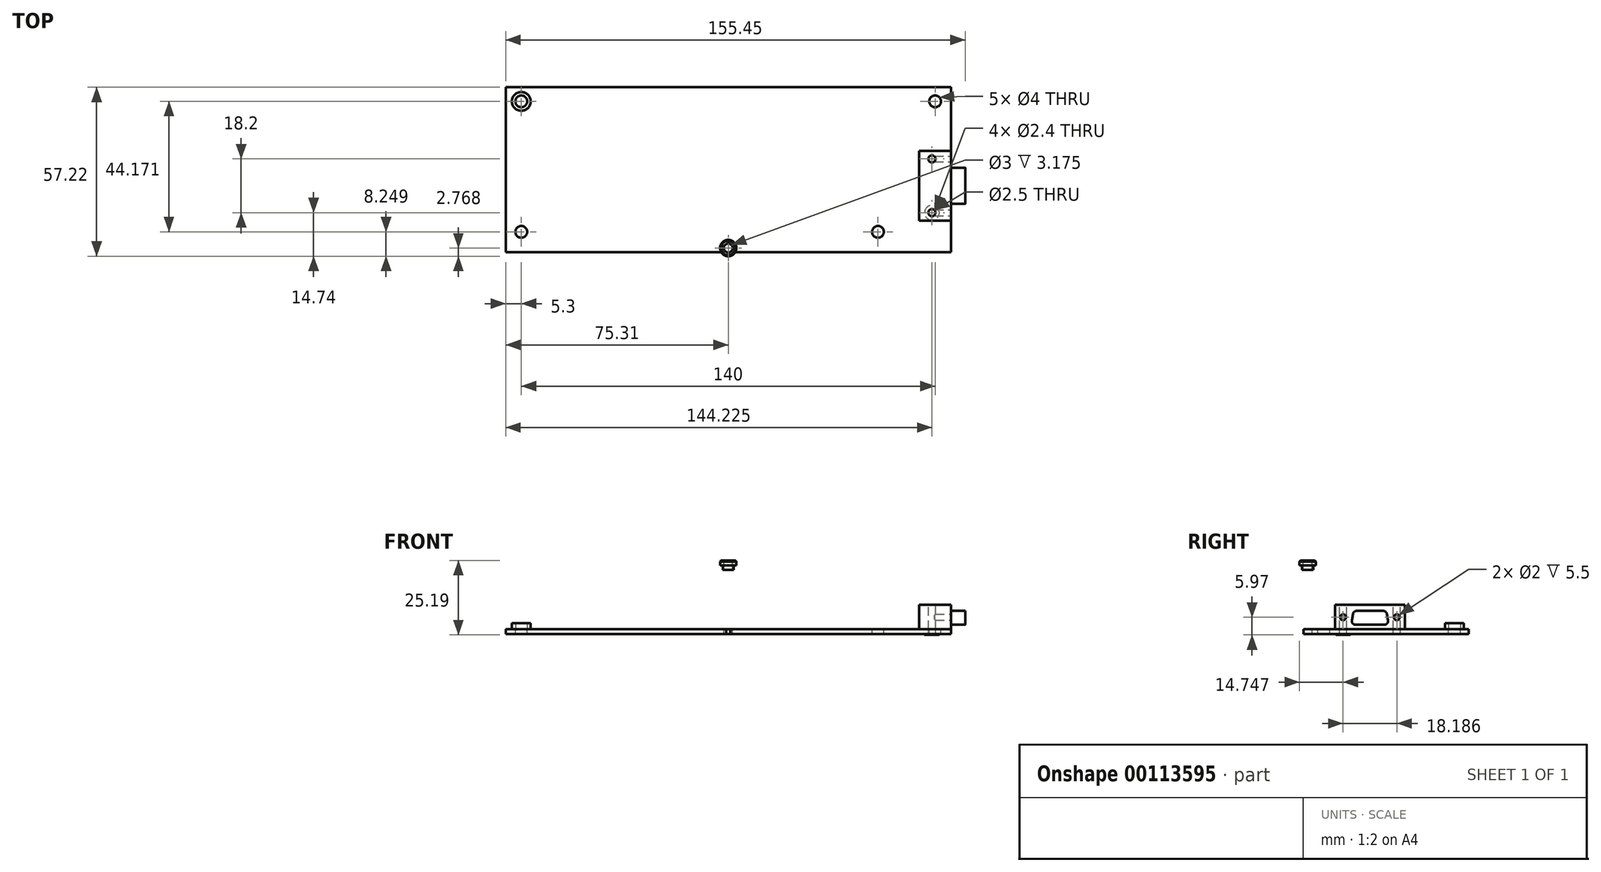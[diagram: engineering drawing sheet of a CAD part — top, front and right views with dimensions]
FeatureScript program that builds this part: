
annotation { "Feature Type Name" : "Feature", "Feature Type Description" : "" }
export const myFeature = defineFeature(function(context is Context, id is Id, definition is map)
    precondition{}
    {
        {
            var Q0;
            Q0=qCreatedBy(makeId("Top.planeOp"),FACE);
            var sketch = newSketch(context, id + "F0", { "sketchPlane" : qUnion([Q0])});
            skLineSegment(sketch, "E0.bottom", {"start": v(75.3, -55.8) * mm, "end": v(-75.31, -55.8) * mm});
            skLineSegment(sketch, "E0.top", {"start": v(75.31, 0) * mm, "end": v(-75.31, 0) * mm});
            skLineSegment(sketch, "E0.left", {"start": v(75.31, -55.8) * mm, "end": v(75.31, 0) * mm});
            skLineSegment(sketch, "E0.right", {"start": v(-75.31, -55.8) * mm, "end": v(-75.31, 0) * mm});
            skPoint(sketch, "E0.middle", {"position": v(0, -27.9) * mm});
            skLineSegment(sketch, "E1", {"start": v(0, 0) * mm, "end": v(0, -55.8) * mm, "construction": true});
            skCircle(sketch, "E2", {"center": v(-70.01, -4.8) * mm, "radius": 2 * mm});
            skCircle(sketch, "E3", {"center": v(-70.01, -48.97) * mm, "radius": 2 * mm});
            skCircle(sketch, "E4", {"center": v(70, -4.8) * mm, "radius": 2 * mm});
            skCircle(sketch, "E5", {"center": v(50.66, -48.97) * mm, "radius": 2 * mm});
            skSolve(sketch);
        }
        {
            var Q0;
            Q0 = qSketchRegion(id + "F0", true);
            extrude(context, id + "F1", {"entities" : qUnion([Q0]), "oppositeDirection" : true, "depth" : 1.57 * mm});
        }
        {
            var Q0;
            Q0=qCreatedBy(makeId("Top.planeOp"),FACE);
            var sketch = newSketch(context, id + "F2", { "sketchPlane" : qUnion([Q0])});
            skCircle(sketch, "E6", {"center": v(-70.01, -4.8) * mm, "radius": 2 * mm});
            skCircle(sketch, "E7", {"center": v(-70.01, -4.8) * mm, "radius": 3.17 * mm});
            skSolve(sketch);
        }
        {
            var Q0;
            Q0 = qSketchRegion(id + "F2", true);
            extrude(context, id + "F3", {"entities" : qUnion([Q0]), "depth" : 2.03 * mm});
        }
        {
            var Q0;
            Q0=makeQuery(id+"F1.opExtrude","CAP_FACE",FACE,{"disambiguationData":[OSD([sQuery(id+"F0.wireOp",EDGE,"E0.bottom"),sQuery(id+"F0.wireOp",EDGE,"E0.top"),sQuery(id+"F0.wireOp",EDGE,"E0.left"),sQuery(id+"F0.wireOp",EDGE,"E0.right"),sQuery(id+"F0.wireOp",EDGE,"E2"),sQuery(id+"F0.wireOp",EDGE,"E3"),sQuery(id+"F0.wireOp",EDGE,"E4"),sQuery(id+"F0.wireOp",EDGE,"E5")])],"isStart":true});
            var sketch = newSketch(context, id + "F4", { "sketchPlane" : qUnion([Q0])});
            skLineSegment(sketch, "E8.bottom", {"start": v(64.52, -21.62) * mm, "end": v(75.31, -21.62) * mm});
            skLineSegment(sketch, "E8.top", {"start": v(64.52, -45.14) * mm, "end": v(75.31, -45.14) * mm});
            skLineSegment(sketch, "E8.left", {"start": v(64.51, -21.62) * mm, "end": v(64.51, -45.14) * mm});
            skLineSegment(sketch, "E8.right", {"start": v(75.31, -21.62) * mm, "end": v(75.31, -45.14) * mm});
            skLineSegment(sketch, "E9", {"start": v(75.31, -33.38) * mm, "end": v(64.52, -33.38) * mm, "construction": true});
            skPoint(sketch, "E9.endSnap0", {"position": v(64.52, -33.38) * mm});
            skSolve(sketch);
        }
        {
            var Q0;
            Q0 = qSketchRegion(id + "F4", true);
            var Q1;
            Q1=sQuery(id+"F4.wireOp",EDGE,"E9");
            extrude(context, id + "F5", {"entities" : qUnion([Q0]), "surfaceEntities" : qUnion([Q1]), "depth" : 8.29 * mm});
        }
        {
            var Q0;
            Q0=makeQuery(id+"F5.opExtrude","SWEPT_FACE",FACE,{"disambiguationData":[OSD([sQuery(id+"F4.wireOp",EDGE,"E8.right")])]});
            var sketch = newSketch(context, id + "F6", { "sketchPlane" : qUnion([Q0])});
            skLineSegment(sketch, "E10.bottom", {"start": v(-37.88, 6.25) * mm, "end": v(-28.88, 6.25) * mm});
            skLineSegment(sketch, "E10.top", {"start": v(-38.26, 1.55) * mm, "end": v(-28.5, 1.55) * mm});
            skLineSegment(sketch, "E11", {"start": v(-39.13, 5.2) * mm, "end": v(-39.51, 3.04) * mm});
            skLineSegment(sketch, "E12", {"start": v(-27.63, 5.2) * mm, "end": v(-27.25, 3.04) * mm});
            skPoint(sketch, "E13.visualSharp", {"position": v(-38.94, 6.25) * mm});
            skArc(sketch, "E13.filletArc", {"start": v(-37.88, 6.25) * mm, "mid": v(-38.7, 5.95) * mm, "end": v(-39.13, 5.2) * mm});
            skPoint(sketch, "E14.visualSharp", {"position": v(-27.82, 6.25) * mm});
            skArc(sketch, "E14.filletArc", {"start": v(-27.63, 5.2) * mm, "mid": v(-28.06, 5.95) * mm, "end": v(-28.88, 6.25) * mm});
            skPoint(sketch, "E15.visualSharp", {"position": v(-39.77, 1.55) * mm});
            skArc(sketch, "E15.filletArc", {"start": v(-39.51, 3.04) * mm, "mid": v(-39.23, 2) * mm, "end": v(-38.26, 1.55) * mm});
            skPoint(sketch, "E16.visualSharp", {"position": v(-26.99, 1.55) * mm});
            skArc(sketch, "E16.filletArc", {"start": v(-28.5, 1.55) * mm, "mid": v(-27.53, 2) * mm, "end": v(-27.25, 3.04) * mm});
            skLineSegment(sketch, "E17", {"start": v(-33.38, 8.29) * mm, "end": v(-33.38, 1.55) * mm, "construction": true});
            skLineSegment(sketch, "E18", {"start": v(-39.36, 3.9) * mm, "end": v(-19.55, 3.9) * mm, "construction": true});
            skPoint(sketch, "E19.orphan", {"position": v(-33.38, 3.9) * mm});
            skPoint(sketch, "E20.orphan", {"position": v(-33.38, 6.25) * mm});
            skSolve(sketch);
        }
        {
            var Q0;
            Q0 = qSketchRegion(id + "F6", true);
            extrude(context, id + "F7", {"entities" : qUnion([Q0]), "operationType" : NewBodyOperationType.ADD, "depth" : 4.83 * mm});
        }
        {
            var Q0;
            Q0=makeQuery(id+"F5.opExtrude","CAP_FACE",FACE,{"disambiguationData":[OSD([sQuery(id+"F4.wireOp",EDGE,"E8.bottom"),sQuery(id+"F4.wireOp",EDGE,"E8.top"),sQuery(id+"F4.wireOp",EDGE,"E8.left"),sQuery(id+"F4.wireOp",EDGE,"E8.right")])],"isStart":false});
            var sketch = newSketch(context, id + "F8", { "sketchPlane" : qUnion([Q0])});
            skCircle(sketch, "E21", {"center": v(68.91, -24.28) * mm, "radius": 1.2 * mm});
            skCircle(sketch, "E22", {"center": v(68.91, -42.48) * mm, "radius": 1.2 * mm});
            skLineSegment(sketch, "E23.0", {"start": v(80.14, -37.88) * mm, "end": v(80.14, -28.88) * mm, "construction": true});
            skLineSegment(sketch, "E24", {"start": v(80.14, -33.38) * mm, "end": v(60.06, -33.38) * mm, "construction": true});
            skSolve(sketch);
        }
        {
            var Q0;
            Q0 = qSketchRegion(id + "F8", true);
            extrude(context, id + "F9", {"entities" : qUnion([Q0]), "operationType" : NewBodyOperationType.REMOVE, "endBound" : BoundingType.THROUGH_ALL, "oppositeDirection" : true, "depth" : 25 * mm});
        }
        {
            var Q0;
            Q0=makeQuery(id+"F1.opExtrude","CAP_FACE",FACE,{"disambiguationData":[OSD([sQuery(id+"F0.wireOp",EDGE,"E0.bottom"),sQuery(id+"F0.wireOp",EDGE,"E0.top"),sQuery(id+"F0.wireOp",EDGE,"E0.left"),sQuery(id+"F0.wireOp",EDGE,"E0.right"),sQuery(id+"F0.wireOp",EDGE,"E2"),sQuery(id+"F0.wireOp",EDGE,"E3"),sQuery(id+"F0.wireOp",EDGE,"E4"),sQuery(id+"F0.wireOp",EDGE,"E5")])],"isStart":false});
            var sketch = newSketch(context, id + "F10", { "sketchPlane" : qUnion([Q0])});
            skCircle(sketch, "E25.0", {"center": v(68.91, 42.48) * mm, "radius": 1.2 * mm});
            skCircle(sketch, "E25.1", {"center": v(68.91, 24.28) * mm, "radius": 1.2 * mm});
            skSolve(sketch);
        }
        {
            var Q0;
            Q0 = qSketchRegion(id + "F10", true);
            extrude(context, id + "F11", {"entities" : qUnion([Q0]), "operationType" : NewBodyOperationType.REMOVE, "endBound" : BoundingType.THROUGH_ALL, "oppositeDirection" : true, "depth" : 25 * mm});
        }
        {
            var Q0;
            Q0=makeQuery(id+"F5.opExtrude","SWEPT_FACE",FACE,{"disambiguationData":[OSD([sQuery(id+"F4.wireOp",EDGE,"E8.right")])]});
            var sketch = newSketch(context, id + "F12", { "sketchPlane" : qUnion([Q0])});
            skCircle(sketch, "E26", {"center": v(-42.47, 4.1) * mm, "radius": 1 * mm});
            skCircle(sketch, "E27", {"center": v(-24.29, 4.1) * mm, "radius": 1 * mm});
            skLineSegment(sketch, "E28", {"start": v(-33.38, 6.25) * mm, "end": v(-33.38, 1.55) * mm, "construction": true});
            skPoint(sketch, "E29.orphan", {"position": v(-33.38, 3.9) * mm});
            skSolve(sketch);
        }
        {
            var Q0;
            Q0 = qSketchRegion(id + "F12", true);
            extrude(context, id + "F13", {"entities" : qUnion([Q0]), "operationType" : NewBodyOperationType.REMOVE, "oppositeDirection" : true, "depth" : 5.5 * mm});
        }
        {
            var Q0;
            Q0=qCreatedBy(makeId("Right.planeOp"),FACE);
            var sketch = newSketch(context, id + "F14", { "sketchPlane" : qUnion([Q0])});
            skLineSegment(sketch, "E30", {"start": v(-54.45, 23.32) * mm, "end": v(-54.45, 20.15) * mm});
            skLineSegment(sketch, "E31", {"start": v(-54.45, 20.15) * mm, "end": v(-52.57, 20.15) * mm});
            skLineSegment(sketch, "E32", {"start": v(-52.57, 20.15) * mm, "end": v(-52.57, 21.67) * mm});
            skLineSegment(sketch, "E33", {"start": v(-52.57, 21.67) * mm, "end": v(-51.68, 21.67) * mm});
            skLineSegment(sketch, "E34", {"start": v(-51.68, 21.67) * mm, "end": v(-51.68, 23.32) * mm});
            skLineSegment(sketch, "E35", {"start": v(-51.68, 23.32) * mm, "end": v(-54.45, 23.32) * mm});
            skLineSegment(sketch, "E36", {"start": v(-54.45, 23.32) * mm, "end": v(-54.45, 41.8) * mm, "construction": true});
            skSolve(sketch);
        }
        {
            var Q0;
            Q0 = qSketchRegion(id + "F14", true);
            var Q1;
            Q1=sQuery(id+"F14.wireOp",EDGE,"E36");
            revolve(context, id + "F15", {"entities" : qUnion([Q0]), "axis" : qUnion([Q1]), "revolveType" : RevolveType.FULL});
        }
        {
            var Q0;
            Q0=makeQuery(id+"F15.opRevolve","SWEPT_EDGE",EDGE,{"disambiguationData":[OSD([sQuery(id+"F14.wireOp",EDGE,"E34"),sQuery(id+"F14.wireOp",EDGE,"E35")])]});
            chamfer(context, id + "F16", {"entities" : qUnion([Q0]), "width" : 0.35 * mm, "tangentPropagation" : true});
        }
        {
            var Q0;
            Q0=makeQuery(id+"F15.opRevolve","SWEPT_FACE",FACE,{"disambiguationData":[OSD([sQuery(id+"F14.wireOp",EDGE,"E35")])]});
            var sketch = newSketch(context, id + "F17", { "sketchPlane" : qUnion([Q0])});
            skCircle(sketch, "E37", {"center": v(0, -54.45) * mm, "radius": 1.5 * mm});
            skSolve(sketch);
        }
        {
            var Q0;
            Q0 = qSketchRegion(id + "F17", true);
            extrude(context, id + "F18", {"entities" : qUnion([Q0]), "operationType" : NewBodyOperationType.REMOVE, "oppositeDirection" : true, "depth" : 25 * mm});
        }
        {
            var Q0;
            Q0=makeQuery(id+"F1.opExtrude","CAP_FACE",FACE,{"disambiguationData":[OSD([sQuery(id+"F0.wireOp",EDGE,"E0.bottom"),sQuery(id+"F0.wireOp",EDGE,"E0.top"),sQuery(id+"F0.wireOp",EDGE,"E0.left"),sQuery(id+"F0.wireOp",EDGE,"E0.right"),sQuery(id+"F0.wireOp",EDGE,"E2"),sQuery(id+"F0.wireOp",EDGE,"E3"),sQuery(id+"F0.wireOp",EDGE,"E4"),sQuery(id+"F0.wireOp",EDGE,"E5")])],"isStart":false});
            var sketch = newSketch(context, id + "F19", { "sketchPlane" : qUnion([Q0])});
            skCircle(sketch, "E38", {"center": v(68.91, 42.48) * mm, "radius": 1.25 * mm});
            skCircle(sketch, "E39", {"center": v(68.91, 42.48) * mm, "radius": 2.5 * mm});
            skSolve(sketch);
        }
        {
            var Q0;
            Q0 = qSketchRegion(id + "F19", true);
            extrude(context, id + "F20", {"entities" : qUnion([Q0]), "depth" : 0.3 * mm});
        }
    });
